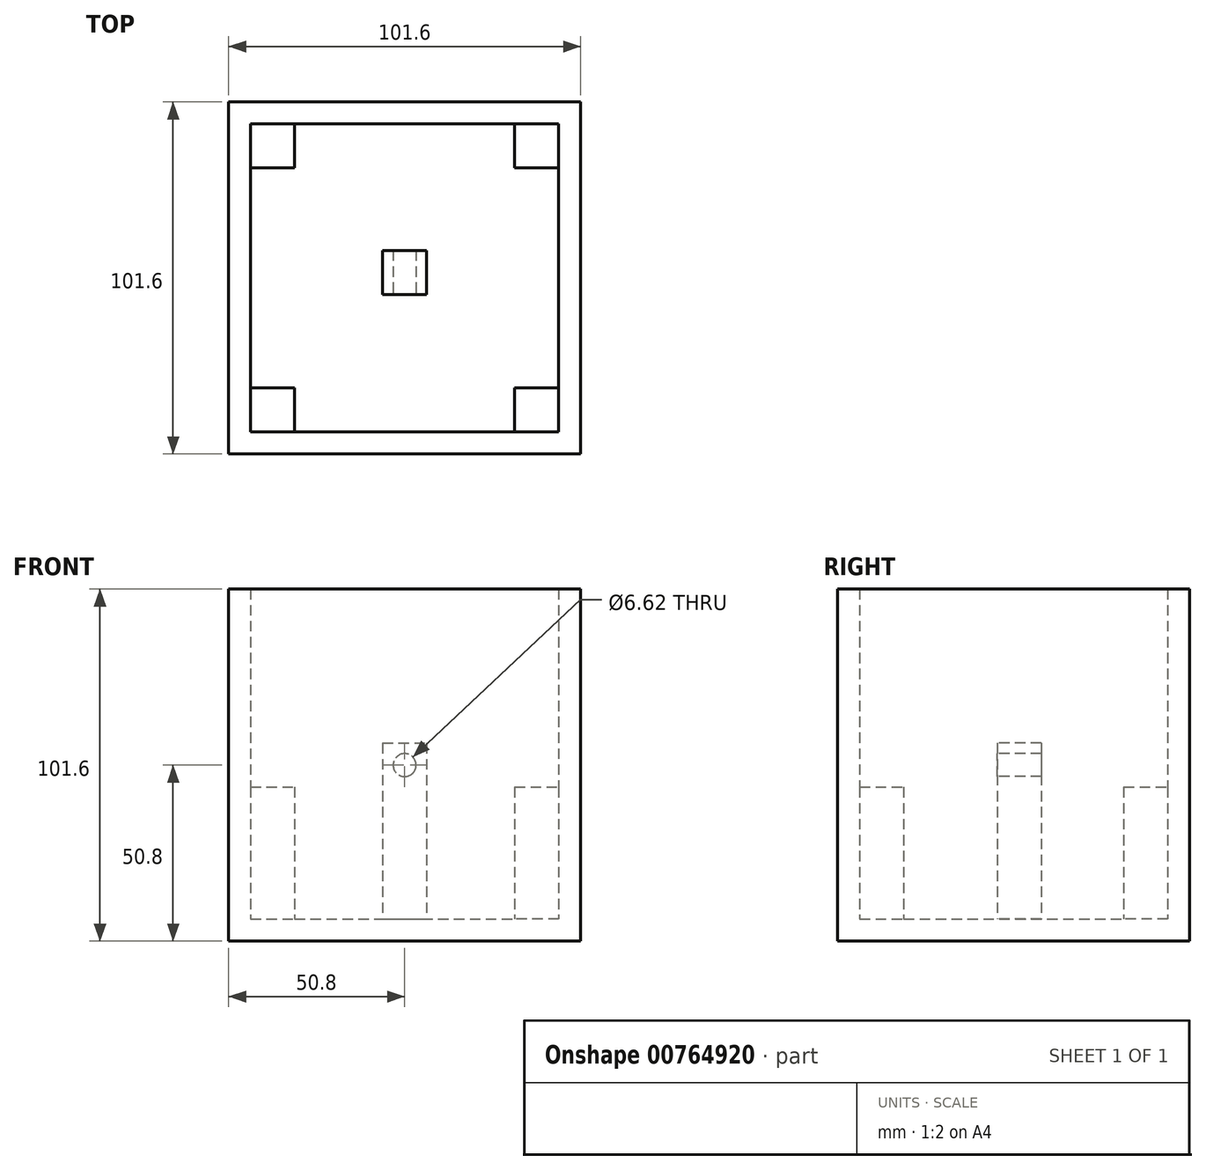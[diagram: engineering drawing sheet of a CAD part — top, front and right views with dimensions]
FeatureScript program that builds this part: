
annotation { "Feature Type Name" : "Feature", "Feature Type Description" : "" }
export const myFeature = defineFeature(function(context is Context, id is Id, definition is map)
    precondition{}
    {
        {
            var Q0;
            Q0=qCreatedBy(makeId("Front.planeOp"),FACE);
            var sketch = newSketch(context, id + "F0", { "sketchPlane" : qUnion([Q0])});
            skLineSegment(sketch, "E0.bottom", {"start": v(-50.8, 50.8) * mm, "end": v(50.8, 50.8) * mm});
            skLineSegment(sketch, "E0.top", {"start": v(-50.8, -50.8) * mm, "end": v(50.8, -50.8) * mm});
            skLineSegment(sketch, "E0.left", {"start": v(-50.8, 50.8) * mm, "end": v(-50.8, -50.8) * mm});
            skLineSegment(sketch, "E0.right", {"start": v(50.8, 50.8) * mm, "end": v(50.8, -50.8) * mm});
            skPoint(sketch, "E0.middle", {"position": v(0, 0) * mm});
            skSolve(sketch);
        }
        {
            var Q0;
            Q0 = qSketchRegion(id + "F0", true);
            extrude(context, id + "F1", {"entities" : qUnion([Q0]), "depth" : 101.6 * mm, "offsetDistance" : 25.4 * mm});
        }
        {
            var Q0;
            Q0=makeQuery(id+"F1.opExtrude","SWEPT_FACE",FACE,{"disambiguationData":[OSD([sQuery(id+"F0.wireOp",EDGE,"E0.bottom")])]});
            shell(context, id + "F2", {"entities" : qUnion([Q0]), "thickness" : 6.35 * mm});
        }
        {
            var Q0;
            Q0=makeQuery(id+"F2.opShell","OFFSET_FACE",FACE,{"disambiguationData":[OSD([sQuery(id+"F0.wireOp",EDGE,"E0.top")])]});
            var sketch = newSketch(context, id + "F3", { "sketchPlane" : qUnion([Q0])});
            skLineSegment(sketch, "E1.bottom", {"start": v(-44.45, -6.35) * mm, "end": v(-31.75, -6.35) * mm});
            skLineSegment(sketch, "E1.top", {"start": v(-44.45, -19.05) * mm, "end": v(-31.75, -19.05) * mm});
            skLineSegment(sketch, "E1.left", {"start": v(-44.45, -6.35) * mm, "end": v(-44.45, -19.05) * mm});
            skLineSegment(sketch, "E1.right", {"start": v(-31.75, -6.35) * mm, "end": v(-31.75, -19.05) * mm});
            skSolve(sketch);
        }
        {
            var Q0;
            Q0=makeQuery(id+"F3.imprint","IMPRINT",FACE,{"disambiguationData":[TD([[makeQuery(id+"F3.imprint","IMPRINT",EDGE,{"derivedFrom":sQuery(id+"F3.wireOp",EDGE,"E1.bottom")}),-1.0]])]});
            extrude(context, id + "F4", {"entities" : qUnion([Q0]), "operationType" : NewBodyOperationType.ADD, "depth" : 38.1 * mm, "offsetDistance" : 25.4 * mm});
        }
        {
            var Q0;
            Q0=makeQuery(id+"F2.opShell","OFFSET_FACE",FACE,{"disambiguationData":[OSD([sQuery(id+"F0.wireOp",EDGE,"E0.top")])]});
            var sketch = newSketch(context, id + "F5", { "sketchPlane" : qUnion([Q0])});
            skLineSegment(sketch, "E2.bottom", {"start": v(44.45, -6.35) * mm, "end": v(31.75, -6.35) * mm});
            skLineSegment(sketch, "E2.top", {"start": v(44.45, -19.05) * mm, "end": v(31.75, -19.05) * mm});
            skLineSegment(sketch, "E2.left", {"start": v(44.45, -6.35) * mm, "end": v(44.45, -19.05) * mm});
            skLineSegment(sketch, "E2.right", {"start": v(31.75, -6.35) * mm, "end": v(31.75, -19.05) * mm});
            skSolve(sketch);
        }
        {
            var Q0;
            Q0 = qSketchRegion(id + "F5", true);
            extrude(context, id + "F6", {"entities" : qUnion([Q0]), "operationType" : NewBodyOperationType.ADD, "depth" : 38.1 * mm, "offsetDistance" : 25.4 * mm});
        }
        {
            var Q0;
            Q0=makeQuery(id+"F2.opShell","OFFSET_FACE",FACE,{"disambiguationData":[OSD([sQuery(id+"F0.wireOp",EDGE,"E0.top")])]});
            var sketch = newSketch(context, id + "F7", { "sketchPlane" : qUnion([Q0])});
            skLineSegment(sketch, "E3.bottom", {"start": v(-44.45, -82.55) * mm, "end": v(-31.75, -82.55) * mm});
            skLineSegment(sketch, "E3.top", {"start": v(-44.45, -95.25) * mm, "end": v(-31.75, -95.25) * mm});
            skLineSegment(sketch, "E3.left", {"start": v(-44.45, -82.55) * mm, "end": v(-44.45, -95.25) * mm});
            skLineSegment(sketch, "E3.right", {"start": v(-31.75, -82.55) * mm, "end": v(-31.75, -95.25) * mm});
            skSolve(sketch);
        }
        {
            var Q0;
            Q0=makeQuery(id+"F7.imprint","IMPRINT",FACE,{"disambiguationData":[TD([[makeQuery(id+"F7.imprint","IMPRINT",EDGE,{"derivedFrom":sQuery(id+"F7.wireOp",EDGE,"E3.bottom")}),-1.0]])]});
            extrude(context, id + "F8", {"entities" : qUnion([Q0]), "operationType" : NewBodyOperationType.ADD, "depth" : 38.1 * mm, "offsetDistance" : 25.4 * mm});
        }
        {
            var Q0;
            Q0=makeQuery(id+"F2.opShell","OFFSET_FACE",FACE,{"disambiguationData":[OSD([sQuery(id+"F0.wireOp",EDGE,"E0.top")])]});
            var sketch = newSketch(context, id + "F9", { "sketchPlane" : qUnion([Q0])});
            skLineSegment(sketch, "E4.bottom", {"start": v(44.45, -95.25) * mm, "end": v(31.75, -95.25) * mm});
            skLineSegment(sketch, "E4.top", {"start": v(44.45, -82.55) * mm, "end": v(31.75, -82.55) * mm});
            skLineSegment(sketch, "E4.left", {"start": v(44.45, -95.25) * mm, "end": v(44.45, -82.55) * mm});
            skLineSegment(sketch, "E4.right", {"start": v(31.75, -95.25) * mm, "end": v(31.75, -82.55) * mm});
            skSolve(sketch);
        }
        {
            var Q0;
            Q0=makeQuery(id+"F9.imprint","IMPRINT",FACE,{"disambiguationData":[TD([[makeQuery(id+"F9.imprint","IMPRINT",EDGE,{"derivedFrom":sQuery(id+"F9.wireOp",EDGE,"E4.bottom")}),1.0]])]});
            extrude(context, id + "F10", {"entities" : qUnion([Q0]), "operationType" : NewBodyOperationType.ADD, "depth" : 38.1 * mm, "offsetDistance" : 25.4 * mm});
        }
        {
            var Q0;
            Q0=makeQuery(id+"F2.opShell","OFFSET_FACE",FACE,{"disambiguationData":[OSD([sQuery(id+"F0.wireOp",EDGE,"E0.top")])]});
            var sketch = newSketch(context, id + "F11", { "sketchPlane" : qUnion([Q0])});
            skLineSegment(sketch, "E5.bottom", {"start": v(-6.35, -42.85) * mm, "end": v(6.35, -42.85) * mm});
            skLineSegment(sketch, "E5.top", {"start": v(-6.35, -55.55) * mm, "end": v(6.35, -55.55) * mm});
            skLineSegment(sketch, "E5.left", {"start": v(-6.35, -42.85) * mm, "end": v(-6.35, -55.55) * mm});
            skLineSegment(sketch, "E5.right", {"start": v(6.35, -42.85) * mm, "end": v(6.35, -55.55) * mm});
            skPoint(sketch, "E5.middle", {"position": v(0, -49.2) * mm});
            skPoint(sketch, "E5.middle.positionSnap0", {"position": v(0, -95.25) * mm});
            skPoint(sketch, "E5.centerSnap0", {"position": v(0, -95.25) * mm});
            skSolve(sketch);
        }
        {
            var Q0;
            Q0=makeQuery(id+"F11.imprint","IMPRINT",FACE,{"disambiguationData":[TD([[makeQuery(id+"F11.imprint","IMPRINT",EDGE,{"derivedFrom":sQuery(id+"F11.wireOp",EDGE,"E5.bottom")}),-1.0]])]});
            extrude(context, id + "F12", {"entities" : qUnion([Q0]), "operationType" : NewBodyOperationType.ADD, "depth" : 50.8 * mm, "offsetDistance" : 25.4 * mm});
        }
        {
            var Q0;
            Q0=makeQuery(id+"F12.opExtrude","SWEPT_FACE",FACE,{"disambiguationData":[OSD([sQuery(id+"F11.wireOp",EDGE,"E5.top")])]});
            var sketch = newSketch(context, id + "F13", { "sketchPlane" : qUnion([Q0])});
            skCircle(sketch, "E6", {"center": v(0, 0) * mm, "radius": 3.31 * mm});
            skSolve(sketch);
        }
        {
            var Q0;
            Q0 = qSketchRegion(id + "F13", true);
            extrude(context, id + "F14", {"entities" : qUnion([Q0]), "operationType" : NewBodyOperationType.REMOVE, "oppositeDirection" : true, "depth" : 25.4 * mm, "offsetDistance" : 25.4 * mm});
        }
    });
